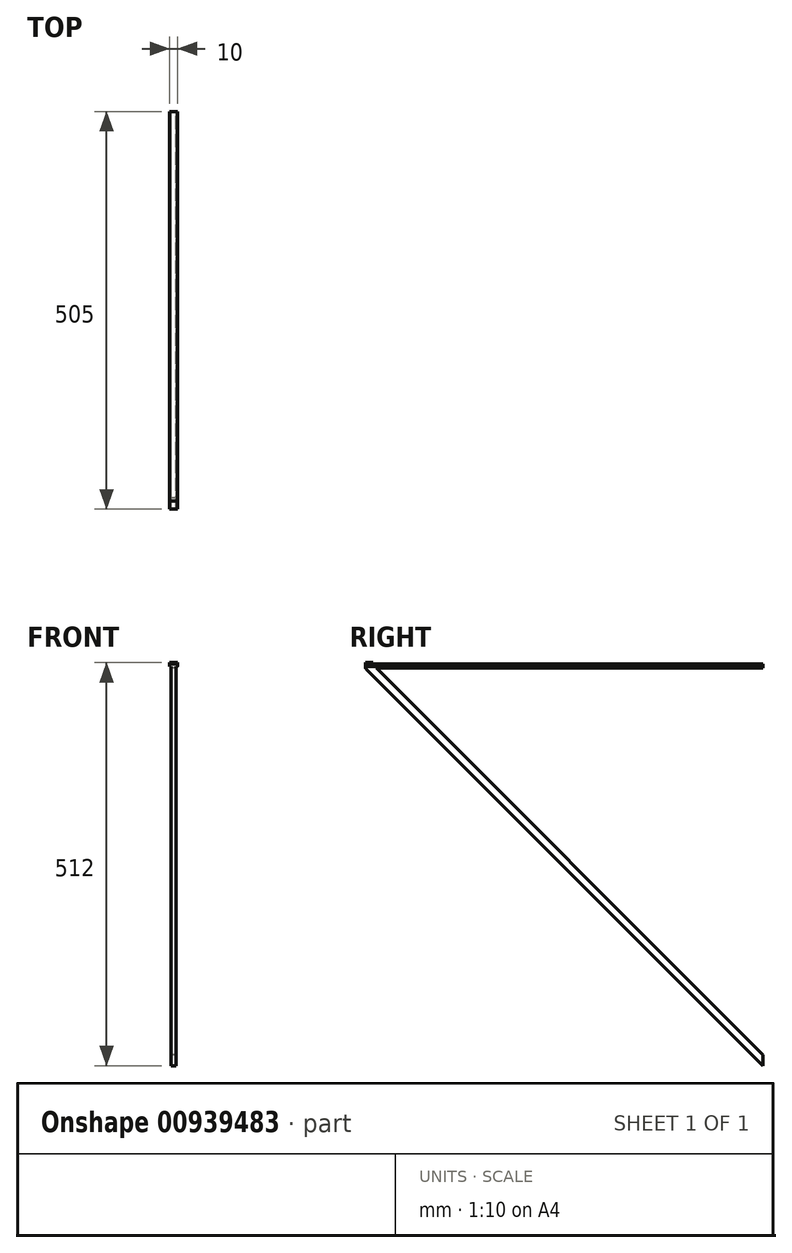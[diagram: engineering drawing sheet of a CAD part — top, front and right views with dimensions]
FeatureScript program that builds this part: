
annotation { "Feature Type Name" : "Feature", "Feature Type Description" : "" }
export const myFeature = defineFeature(function(context is Context, id is Id, definition is map)
    precondition{}
    {
        {
            var Q0;
            Q0=qCreatedBy(makeId("Front.planeOp"),FACE);
            var sketch = newSketch(context, id + "F0", { "sketchPlane" : qUnion([Q0])});
            skLineSegment(sketch, "E0", {"start": v(-5, 0) * mm, "end": v(-5, 3) * mm});
            skLineSegment(sketch, "E1", {"start": v(-5, 3) * mm, "end": v(5, 3) * mm});
            skLineSegment(sketch, "E2", {"start": v(5, 3) * mm, "end": v(5, 0) * mm});
            skLineSegment(sketch, "E3", {"start": v(5, 0) * mm, "end": v(-5, 0) * mm});
            skLineSegment(sketch, "E4", {"start": v(-3, 0) * mm, "end": v(-3, -2) * mm});
            skLineSegment(sketch, "E5", {"start": v(-3, -2) * mm, "end": v(3, -2) * mm});
            skLineSegment(sketch, "E6", {"start": v(3, -2) * mm, "end": v(3, 0) * mm});
            skPoint(sketch, "E7", {"position": v(0, 0) * mm});
            skSolve(sketch);
        }
        {
            var Q0;
            {var subQ0=sQuery(id+"F0.wireOp",EDGE,"E4");Q0=makeQuery(id+"F0.imprint","IMPRINT",FACE,{"disambiguationData":[TD([[makeQuery(id+"F0.imprint","IMPRINT",EDGE,{"derivedFrom":subQ0}),1.0]])]});}
            var Q1;
            {var subQ3=sQuery(id+"F0.wireOp",EDGE,"E0");Q1=makeQuery(id+"F0.imprint","IMPRINT",FACE,{"disambiguationData":[TD([[makeQuery(id+"F0.imprint","IMPRINT",EDGE,{"derivedFrom":subQ3}),-1.0]])]});}
            extrude(context, id + "F1", {"entities" : qUnion([Q0, Q1]), "depth" : 505 * mm, "offsetDistance" : 25 * mm});
        }
        {
            var Q0;
            Q0=makeQuery(id+"F1.opExtrude","SWEPT_FACE",FACE,{"disambiguationData":[OSD([sQuery(id+"F0.wireOp",EDGE,"E4")])]});
            var sketch = newSketch(context, id + "F2", { "sketchPlane" : qUnion([Q0])});
            skLineSegment(sketch, "E8", {"start": v(505, -2) * mm, "end": v(0, -507) * mm});
            skLineSegment(sketch, "E9", {"start": v(0, -507) * mm, "end": v(0, -493) * mm});
            skLineSegment(sketch, "E10", {"start": v(0, -493) * mm, "end": v(491, -2) * mm});
            skSolve(sketch);
        }
        {
            var Q0;
            {var subQ0=sQuery(id+"F2.wireOp",EDGE,"E8");Q0=makeQuery(id+"F2.imprint","IMPRINT",FACE,{"disambiguationData":[TD([[makeQuery(id+"F2.imprint","IMPRINT",EDGE,{"derivedFrom":subQ0}),-1.0]])]});}
            var Q1;
            {var subQ0=sQuery(id+"F2.wireOp",EDGE,"E10");var subQ3=sQuery(id+"F2.wireOp",EDGE,"lxwbxgLq-BOKp-7qzk-AFzH-953oZaWUqetL");var subQ4=makeQuery(id+"F2.imprint","INTERSECT",VERTEX,{"disambiguationData":[OD(1.0)],"derivedFrom":[subQ0,subQ3]});Q1=makeQuery(id+"F2.imprint","IMPRINT",FACE,{"disambiguationData":[TD([[makeQuery(id+"F2.imprint","IMPRINT",EDGE,{"disambiguationData":[TD([[subQ4,-1.0]])],"derivedFrom":subQ0}),1.0]])]});}
            var Q2;
            {var subQ0=sQuery(id+"F2.wireOp",EDGE,"lxwbxgLq-BOKp-7qzk-AFzH-953oZaWUqetL");var subQ1=sQuery(id+"F2.wireOp",EDGE,"E10");var subQ2=makeQuery(id+"F2.imprint","INTERSECT",VERTEX,{"disambiguationData":[OD(0.0)],"derivedFrom":[subQ1,subQ0]});Q2=makeQuery(id+"F2.imprint","IMPRINT",FACE,{"disambiguationData":[TD([[makeQuery(id+"F2.imprint","IMPRINT",EDGE,{"disambiguationData":[TD([[subQ2,-1.0]])],"derivedFrom":subQ1}),-1.0]])]});}
            var Q3;
            {var subQ0=sQuery(id+"F2.wireOp",EDGE,"E10");var subQ9=sQuery(id+"F2.wireOp",EDGE,"SXYTpxOy-1LzB-IjTZ-bXXj-8hcJFfRafIov");var subQ11=makeQuery(id+"F2.imprint","INTERSECT",VERTEX,{"derivedFrom":[subQ0,subQ9]});Q3=makeQuery(id+"F2.imprint","IMPRINT",FACE,{"disambiguationData":[TD([[makeQuery(id+"F2.imprint","IMPRINT",EDGE,{"disambiguationData":[TD([[subQ11,-1.0]])],"derivedFrom":subQ0}),-1.0]])]});}
            var Q4;
            {var subQ0=sQuery(id+"F2.wireOp",EDGE,"7C1dEwzO-nGoi-hHsn-EZ6T-vzB99gRt0dMv");var subQ1=sQuery(id+"F2.wireOp",EDGE,"E10");var subQ2=makeQuery(id+"F2.imprint","INTERSECT",VERTEX,{"derivedFrom":[subQ1,subQ0]});Q4=makeQuery(id+"F2.imprint","IMPRINT",FACE,{"disambiguationData":[TD([[makeQuery(id+"F2.imprint","IMPRINT",EDGE,{"disambiguationData":[TD([[subQ2,-1.0]])],"derivedFrom":subQ1}),1.0]])]});}
            var Q5;
            {var subQ0=sQuery(id+"F2.wireOp",EDGE,"KrNmojeR-vB4b-axkl-UfPT-1YWsb5pYtXaG");var subQ1=sQuery(id+"F2.wireOp",EDGE,"E10");var subQ2=makeQuery(id+"F2.imprint","INTERSECT",VERTEX,{"derivedFrom":[subQ1,subQ0]});Q5=makeQuery(id+"F2.imprint","IMPRINT",FACE,{"disambiguationData":[TD([[makeQuery(id+"F2.imprint","IMPRINT",EDGE,{"disambiguationData":[TD([[subQ2,-1.0]])],"derivedFrom":subQ1}),1.0]])]});}
            extrude(context, id + "F3", {"entities" : qUnion([Q0, Q1, Q2, Q3, Q4, Q5]), "oppositeDirection" : true, "depth" : 6 * mm, "offsetDistance" : 25 * mm});
        }
        {
            var Q0;
            Q0=makeQuery(id+"F1.opExtrude","SWEPT_BODY",BODY,{"disambiguationData":[OSD([sQuery(id+"F0.wireOp",EDGE,"E0"),sQuery(id+"F0.wireOp",EDGE,"E1"),sQuery(id+"F0.wireOp",EDGE,"E2"),sQuery(id+"F0.wireOp",EDGE,"E3"),sQuery(id+"F0.wireOp",EDGE,"E4"),sQuery(id+"F0.wireOp",EDGE,"E5"),sQuery(id+"F0.wireOp",EDGE,"E6")])]});
            var Q1;
            Q1=makeQuery(id+"F3.opExtrude","SWEPT_BODY",BODY,{"disambiguationData":[OSD([sQuery(id+"F0.wireOp",EDGE,"E4"),sQuery(id+"F0.wireOp",EDGE,"E5"),sQuery(id+"F2.wireOp",EDGE,"E8"),sQuery(id+"F2.wireOp",EDGE,"E9"),sQuery(id+"F2.wireOp",EDGE,"E10")])]});
            booleanBodies(context, id + "F4", {"operationType" : BooleanOperationType.UNION, "tools" : qUnion([Q0, Q1])});
        }
        {
            var Q0;
            Q0=makeQuery(id+"F1.opExtrude","SWEPT_FACE",FACE,{"disambiguationData":[OSD([sQuery(id+"F0.wireOp",EDGE,"E0")])]});
            var sketch = newSketch(context, id + "F5", { "sketchPlane" : qUnion([Q0])});
            skLineSegment(sketch, "E11", {"start": v(505, 3) * mm, "end": v(495, 3) * mm});
            skLineSegment(sketch, "E12", {"start": v(495, 3) * mm, "end": v(495, 5) * mm});
            skLineSegment(sketch, "E13", {"start": v(495, 5) * mm, "end": v(505, 5) * mm});
            skLineSegment(sketch, "E14", {"start": v(505, 5) * mm, "end": v(505, 3) * mm});
            skPoint(sketch, "E15", {"position": v(500, 5) * mm});
            skSolve(sketch);
        }
        {
            var Q0;
            Q0=makeQuery(id+"F5.imprint","IMPRINT",FACE,{"disambiguationData":[TD([[makeQuery(id+"F5.imprint","IMPRINT",EDGE,{"derivedFrom":sQuery(id+"F5.wireOp",EDGE,"E11")}),-1.0]])]});
            extrude(context, id + "F6", {"entities" : qUnion([Q0]), "oppositeDirection" : true, "depth" : 10 * mm, "offsetDistance" : 25 * mm});
        }
        {
            var Q0;
            Q0=makeQuery(id+"F6.opExtrude","SWEPT_EDGE",EDGE,{"disambiguationData":[OSD([sQuery(id+"F0.wireOp",EDGE,"E0"),sQuery(id+"F0.wireOp",EDGE,"E1"),sQuery(id+"F5.wireOp",EDGE,"E11"),sQuery(id+"F5.wireOp",EDGE,"E12")])]});
            var Q1;
            {var subQ0=sQuery(id+"F0.wireOp",EDGE,"E5");Q1=makeQuery(id+"F4.opBoolean","MERGE",EDGE,{"derivedFrom":[makeQuery(id+"F1.opExtrude","CAP_EDGE",EDGE,{"disambiguationData":[OSD([subQ0])],"isStart":false}),makeQuery(id+"F3.opExtrude","SWEPT_EDGE",EDGE,{"disambiguationData":[OSD([sQuery(id+"F0.wireOp",EDGE,"E4"),subQ0,sQuery(id+"F2.wireOp",EDGE,"E8")])]})]});}
            var Q2;
            Q2=makeQuery(id+"F3.opExtrude","SWEPT_EDGE",EDGE,{"disambiguationData":[OSD([sQuery(id+"F0.wireOp",EDGE,"E4"),sQuery(id+"F0.wireOp",EDGE,"E5"),sQuery(id+"F2.wireOp",EDGE,"E10")])]});
            fillet(context, id + "F7", {"entities" : qUnion([Q0, Q1, Q2]), "radius" : 5 * mm, "tangentPropagation" : true, "allowEdgeOverflow" : false});
        }
    });
